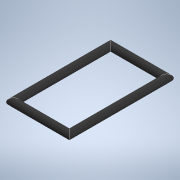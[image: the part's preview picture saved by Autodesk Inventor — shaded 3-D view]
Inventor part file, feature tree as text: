
AUTODESK INVENTOR PART (.ipt)
format: ipt  version: 2022 (Build 260153000, 153)  size: 108,544 bytes
history: native  units: in
note: dims shown in document units (in); Inventor stores cm internally (conversion verified against a paired STEP export)
features: other x2, sketch x2, sweep x1
ambient origin geometry x8: Origin, YZ Plane, XZ Plane, XY Plane, X Axis, Y Axis, Z Axis, Center Point
bodies: Solid1 (feature_tree)
feature tree (5):
  other  "Annotations"
  sweep  "Sweep1"
  sketch  "Sketch1"  dims[d0=1.393in d1=0.8024in]
  sketch  "Sketch2"  dims[d2=0.103in d3=0.0in d4=0.0in]
  other  "General Note 1"
